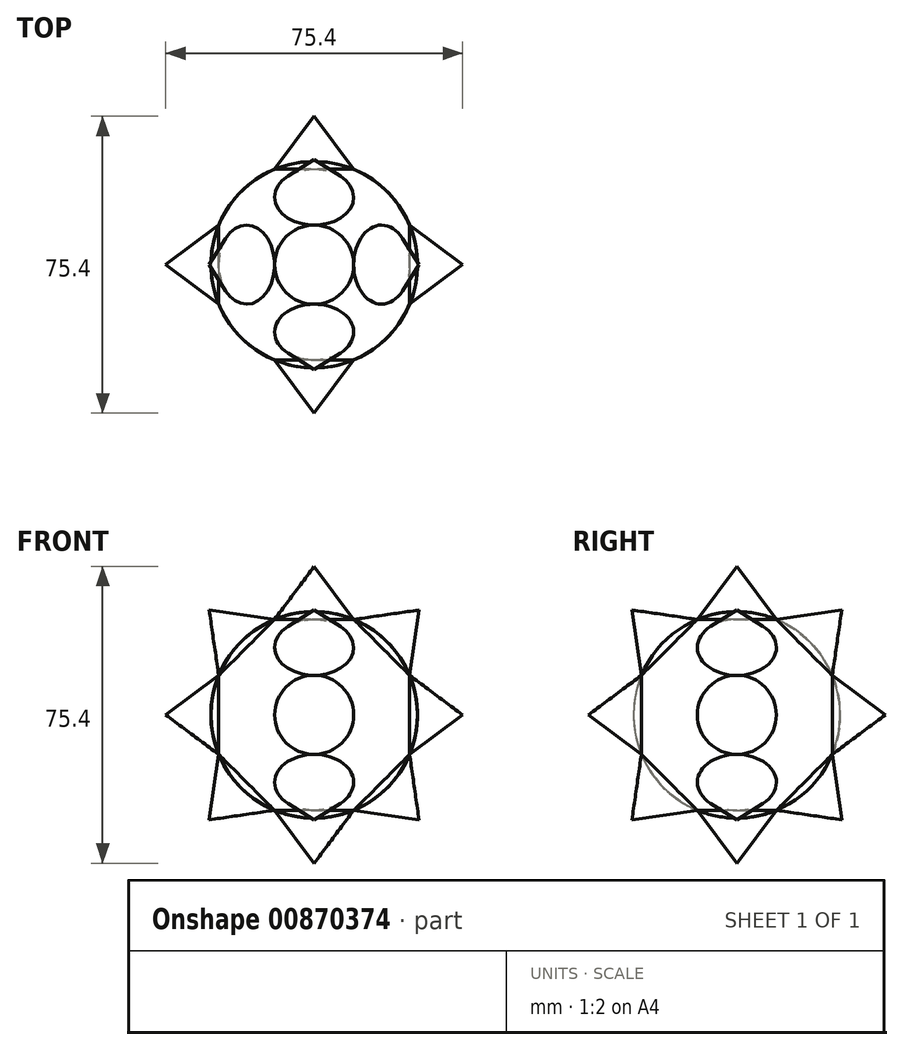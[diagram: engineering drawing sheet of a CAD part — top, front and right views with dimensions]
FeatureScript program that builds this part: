
annotation { "Feature Type Name" : "Feature", "Feature Type Description" : "" }
export const myFeature = defineFeature(function(context is Context, id is Id, definition is map)
    precondition{}
    {
        {
            var Q0;
            Q0=qCreatedBy(makeId("Front.planeOp"),FACE);
            var sketch = newSketch(context, id + "F0", { "sketchPlane" : qUnion([Q0])});
            skLineSegment(sketch, "E0", {"start": v(0, 26.24) * mm, "end": v(0, 37.7) * mm});
            skLineSegment(sketch, "E1.4.0", {"start": v(0, -26.24) * mm, "end": v(0, -37.7) * mm});
            skPoint(sketch, "E1.center", {"position": v(0, 0) * mm});
            skLineSegment(sketch, "E2", {"start": v(0, 37.7) * mm, "end": v(10.04, 24.24) * mm});
            skLineSegment(sketch, "E3", {"start": v(0, -37.7) * mm, "end": v(10.04, -24.24) * mm});
            skArc(sketch, "E4", {"start": v(0, -26.24) * mm, "mid": v(26.24, 0) * mm, "end": v(0, 26.24) * mm});
            skLineSegment(sketch, "E5", {"start": v(0, 26.24) * mm, "end": v(0, -26.24) * mm});
            skSolve(sketch);
        }
        {
            var Q0;
            {var subQ0=sQuery(id+"F0.wireOp",EDGE,"E5");Q0=makeQuery(id+"F0.imprint","IMPRINT",FACE,{"disambiguationData":[TD([[makeQuery(id+"F0.imprint","IMPRINT",EDGE,{"derivedFrom":subQ0}),1.0]])]});}
            var Q1;
            {var subQ0=sQuery(id+"F0.wireOp",EDGE,"E0");Q1=makeQuery(id+"F0.imprint","IMPRINT",FACE,{"disambiguationData":[TD([[makeQuery(id+"F0.imprint","IMPRINT",EDGE,{"derivedFrom":subQ0}),-1.0]])]});}
            var Q2;
            {var subQ0=sQuery(id+"F0.wireOp",EDGE,"E1.4.0");Q2=makeQuery(id+"F0.imprint","IMPRINT",FACE,{"disambiguationData":[TD([[makeQuery(id+"F0.imprint","IMPRINT",EDGE,{"derivedFrom":subQ0}),1.0]])]});}
            var Q3;
            Q3=sQuery(id+"F0.wireOp",EDGE,"E0");
            revolve(context, id + "F1", {"surfaceOperationType" : NewSurfaceOperationType.NEW, "entities" : qUnion([Q0, Q1, Q2]), "axis" : qUnion([Q3]), "revolveType" : RevolveType.FULL});
        }
        {
            var Q0;
            Q0=qCreatedBy(makeId("Front.planeOp"),FACE);
            var sketch = newSketch(context, id + "F2", { "sketchPlane" : qUnion([Q0])});
            skLineSegment(sketch, "E6", {"start": v(26.24, 0) * mm, "end": v(37.7, 0) * mm});
            skLineSegment(sketch, "E7.4.0", {"start": v(-26.24, 0) * mm, "end": v(-37.7, 0) * mm});
            skPoint(sketch, "E7.center", {"position": v(0, 0) * mm});
            skLineSegment(sketch, "E8", {"start": v(37.7, 0) * mm, "end": v(24.24, -10.04) * mm});
            skLineSegment(sketch, "E9", {"start": v(-37.7, 0) * mm, "end": v(-24.24, -10.04) * mm});
            skArc(sketch, "E10", {"start": v(-26.24, 0) * mm, "mid": v(0, -26.24) * mm, "end": v(26.24, 0) * mm});
            skLineSegment(sketch, "E11", {"start": v(26.24, 0) * mm, "end": v(-26.24, 0) * mm});
            skSolve(sketch);
        }
        {
            var Q0;
            Q0 = qSketchRegion(id + "F2", true);
            var Q1;
            Q1=sQuery(id+"F2.wireOp",EDGE,"E11");
            revolve(context, id + "F3", {"surfaceOperationType" : NewSurfaceOperationType.NEW, "entities" : qUnion([Q0]), "axis" : qUnion([Q1]), "revolveType" : RevolveType.FULL});
        }
        {
            var Q0;
            Q0=qCreatedBy(makeId("Right.planeOp"),FACE);
            var sketch = newSketch(context, id + "F4", { "sketchPlane" : qUnion([Q0])});
            skLineSegment(sketch, "E12", {"start": v(-26.24, 0) * mm, "end": v(-37.7, 0) * mm});
            skLineSegment(sketch, "E13.4.0", {"start": v(26.24, 0) * mm, "end": v(37.7, 0) * mm});
            skPoint(sketch, "E13.center", {"position": v(0, 0) * mm});
            skLineSegment(sketch, "E14", {"start": v(-37.7, 0) * mm, "end": v(-24.24, 10.04) * mm});
            skLineSegment(sketch, "E15", {"start": v(37.7, 0) * mm, "end": v(24.24, 10.04) * mm});
            skArc(sketch, "E16", {"start": v(26.24, 0) * mm, "mid": v(0, 26.24) * mm, "end": v(-26.24, 0) * mm});
            skLineSegment(sketch, "E17", {"start": v(-26.24, 0) * mm, "end": v(26.24, 0) * mm});
            skSolve(sketch);
        }
        {
            var Q0;
            Q0 = qSketchRegion(id + "F4", true);
            var Q1;
            Q1=sQuery(id+"F4.wireOp",EDGE,"E17");
            revolve(context, id + "F5", {"surfaceOperationType" : NewSurfaceOperationType.NEW, "entities" : qUnion([Q0]), "axis" : qUnion([Q1]), "revolveType" : RevolveType.FULL});
        }
        {
            var Q0;
            Q0=qCreatedBy(makeId("Front.planeOp"),FACE);
            var sketch = newSketch(context, id + "F6", { "sketchPlane" : qUnion([Q0])});
            skLineSegment(sketch, "E18", {"start": v(18.56, 18.56) * mm, "end": v(26.66, 26.66) * mm});
            skLineSegment(sketch, "E19.4.0", {"start": v(-18.56, -18.56) * mm, "end": v(-26.66, -26.66) * mm});
            skPoint(sketch, "E19.center", {"position": v(0, 0) * mm});
            skLineSegment(sketch, "E20", {"start": v(26.66, 26.66) * mm, "end": v(24.24, 10.04) * mm});
            skLineSegment(sketch, "E21", {"start": v(-26.66, -26.66) * mm, "end": v(-10.04, -24.24) * mm});
            skArc(sketch, "E22", {"start": v(-18.56, -18.56) * mm, "mid": v(18.56, -18.56) * mm, "end": v(18.56, 18.56) * mm});
            skLineSegment(sketch, "E23", {"start": v(18.56, 18.56) * mm, "end": v(-18.56, -18.56) * mm});
            skSolve(sketch);
        }
        {
            var Q0;
            Q0 = qSketchRegion(id + "F6", true);
            var Q1;
            Q1=sQuery(id+"F6.wireOp",EDGE,"E23");
            revolve(context, id + "F7", {"surfaceOperationType" : NewSurfaceOperationType.NEW, "entities" : qUnion([Q0]), "axis" : qUnion([Q1]), "revolveType" : RevolveType.FULL});
        }
        {
            var Q0;
            Q0=qCreatedBy(makeId("Front.planeOp"),FACE);
            var sketch = newSketch(context, id + "F8", { "sketchPlane" : qUnion([Q0])});
            skLineSegment(sketch, "E24", {"start": v(18.56, -18.56) * mm, "end": v(26.66, -26.66) * mm});
            skLineSegment(sketch, "E25.4.0", {"start": v(-18.56, 18.56) * mm, "end": v(-26.66, 26.66) * mm});
            skPoint(sketch, "E25.center", {"position": v(0, 0) * mm});
            skLineSegment(sketch, "E26", {"start": v(26.66, -26.66) * mm, "end": v(10.04, -24.24) * mm});
            skLineSegment(sketch, "E27", {"start": v(-26.66, 26.66) * mm, "end": v(-24.24, 10.04) * mm});
            skArc(sketch, "E28", {"start": v(-18.56, 18.56) * mm, "mid": v(-18.56, -18.56) * mm, "end": v(18.56, -18.56) * mm});
            skLineSegment(sketch, "E29", {"start": v(18.56, -18.56) * mm, "end": v(-18.56, 18.56) * mm});
            skSolve(sketch);
        }
        {
            var Q0;
            Q0 = qSketchRegion(id + "F8", true);
            var Q1;
            Q1=sQuery(id+"F8.wireOp",EDGE,"E29");
            revolve(context, id + "F9", {"surfaceOperationType" : NewSurfaceOperationType.NEW, "entities" : qUnion([Q0]), "axis" : qUnion([Q1]), "revolveType" : RevolveType.FULL});
        }
        {
            var Q0;
            Q0=qCreatedBy(makeId("Right.planeOp"),FACE);
            var sketch = newSketch(context, id + "F10", { "sketchPlane" : qUnion([Q0])});
            skLineSegment(sketch, "E30", {"start": v(18.56, 18.56) * mm, "end": v(26.66, 26.66) * mm});
            skLineSegment(sketch, "E31.4.0", {"start": v(-18.56, -18.56) * mm, "end": v(-26.66, -26.66) * mm});
            skPoint(sketch, "E31.center", {"position": v(0, 0) * mm});
            skLineSegment(sketch, "E32", {"start": v(26.66, 26.66) * mm, "end": v(24.24, 10.04) * mm});
            skLineSegment(sketch, "E33", {"start": v(-26.66, -26.66) * mm, "end": v(-10.04, -24.24) * mm});
            skArc(sketch, "E34", {"start": v(-18.56, -18.56) * mm, "mid": v(18.56, -18.56) * mm, "end": v(18.56, 18.56) * mm});
            skLineSegment(sketch, "E35", {"start": v(18.56, 18.56) * mm, "end": v(-18.56, -18.56) * mm});
            skSolve(sketch);
        }
        {
            var Q0;
            Q0 = qSketchRegion(id + "F10", true);
            var Q1;
            Q1=sQuery(id+"F10.wireOp",EDGE,"E30");
            revolve(context, id + "F11", {"surfaceOperationType" : NewSurfaceOperationType.NEW, "entities" : qUnion([Q0]), "axis" : qUnion([Q1]), "revolveType" : RevolveType.FULL});
        }
        {
            var Q0;
            Q0=qCreatedBy(makeId("Right.planeOp"),FACE);
            var sketch = newSketch(context, id + "F12", { "sketchPlane" : qUnion([Q0])});
            skLineSegment(sketch, "E36", {"start": v(18.56, -18.56) * mm, "end": v(26.66, -26.66) * mm});
            skLineSegment(sketch, "E37.4.0", {"start": v(-18.56, 18.56) * mm, "end": v(-26.66, 26.66) * mm});
            skPoint(sketch, "E37.center", {"position": v(0, 0) * mm});
            skLineSegment(sketch, "E38", {"start": v(26.66, -26.66) * mm, "end": v(10.04, -24.24) * mm});
            skLineSegment(sketch, "E39", {"start": v(-26.66, 26.66) * mm, "end": v(-24.24, 10.04) * mm});
            skArc(sketch, "E40", {"start": v(-18.56, 18.56) * mm, "mid": v(-18.56, -18.56) * mm, "end": v(18.56, -18.56) * mm});
            skLineSegment(sketch, "E41", {"start": v(18.56, -18.56) * mm, "end": v(-18.56, 18.56) * mm});
            skSolve(sketch);
        }
        {
            var Q0;
            Q0 = qSketchRegion(id + "F12", true);
            var Q1;
            Q1=sQuery(id+"F12.wireOp",EDGE,"E37.4.0");
            revolve(context, id + "F13", {"surfaceOperationType" : NewSurfaceOperationType.NEW, "entities" : qUnion([Q0]), "axis" : qUnion([Q1]), "revolveType" : RevolveType.FULL});
        }
    });
